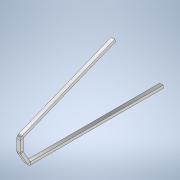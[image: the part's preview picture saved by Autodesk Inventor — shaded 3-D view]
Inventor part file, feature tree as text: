
AUTODESK INVENTOR PART (.ipt)
format: ipt  version: 2020.1 (Build 241239000, 239)  size: 144,384 bytes
history: native  units: mm
features: sheet_metal_op x10, sketch x4, other x4
ambient origin geometry x8: Origin, YZ Plane, XZ Plane, XY Plane, X Axis, Y Axis, Z Axis, Center Point
bodies: Solid1 (feature_tree)
feature tree (18):
  sheet_metal_op  "Face1"
  sheet_metal_op  "Flange1"
  sheet_metal_op  "Flange2"
  sheet_metal_op  "Flange3"
  sketch  "Sketch1"  dims[d0=0.448mm]
  other  "Plate1"
  sketch  "Sketch2"  dims[d1=16.85mm]
  other  "Plate2"
  sheet_metal_op  "Bend1"
  sheet_metal_op  "Corner1"
  sketch  "Sketch3"  dims[d2=0.35mm]
  other  "Plate3"
  sheet_metal_op  "Bend2"
  sheet_metal_op  "Corner2"
  sketch  "Sketch4"  dims[d3=0.35mm d4=0.175mm d5=0.7mm d6=0.1mm d7=2.055mm d8=60.0deg d9=0.1mm d10=1.4mm d11=0.35mm d12=0.1mm d13=0.35mm d14=0.175mm d15=0.7mm d16=0.1mm d17=1.4685mm d18=30.0deg d19=0.1mm d20=1.4mm d21=0.35mm d22=0.1mm d23=0.35mm d24=0.175mm d25=0.7mm d26=0.1mm d27=12.95mm d28=11.868239mm d29=0.1mm d30=1.4mm d31=0.35mm d32=0.1mm]
  other  "Plate4"
  sheet_metal_op  "Bend3"
  sheet_metal_op  "Corner3"
